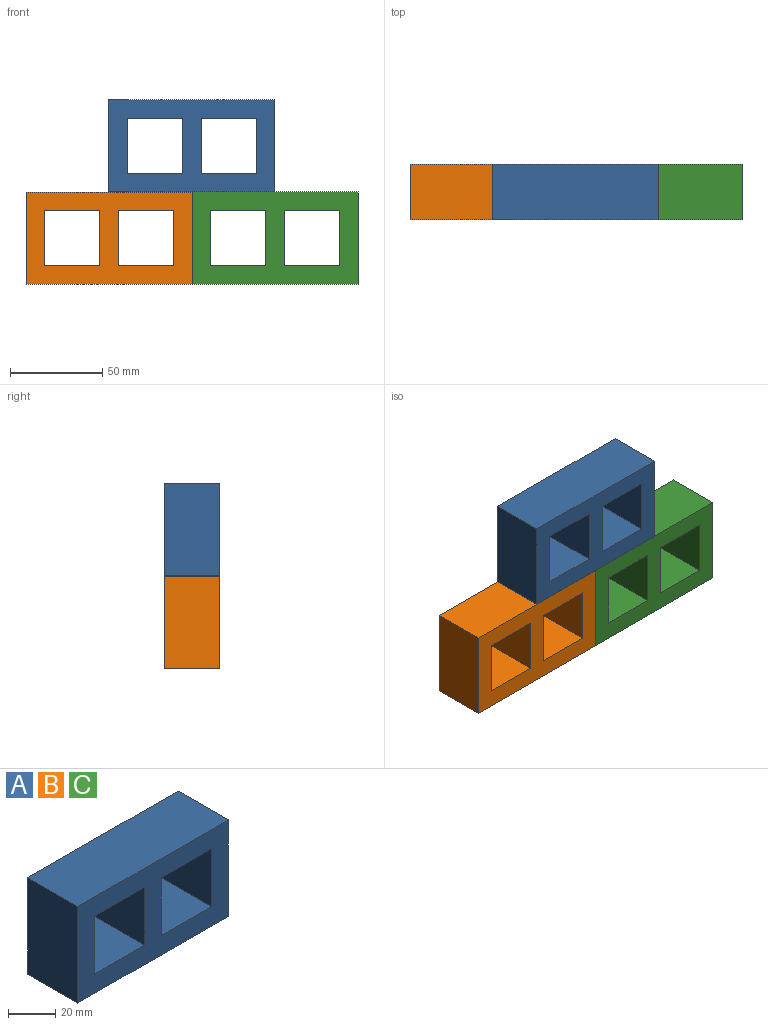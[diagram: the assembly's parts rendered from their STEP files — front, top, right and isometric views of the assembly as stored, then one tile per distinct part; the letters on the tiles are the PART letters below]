
ASSEMBLY  parts=3 mates=2
PART A: 14 faces, bbox 90x30x50 mm
  f0: plane 90x30mm, normal (0,0,1), area 2700mm2, adj f1,f11,f12,f13
  f1: plane 50x30mm, normal (-1,0,0), area 1500mm2, adj f0,f2,f12,f13
  f2: plane 90x30mm, normal (0,0,-1), area 2700mm2, adj f1,f11,f12,f13
  f3: plane 30x30mm, normal (1,0,0), area 900mm2, adj f4,f9,f12,f13
  f4: plane 30x30mm, normal (0,0,-1), area 900mm2, adj f3,f5,f12,f13
  f5: plane 30x30mm, normal (-1,0,0), area 900mm2, adj f4,f9,f12,f13
  f6: plane 30x30mm, normal (1,0,0), area 900mm2, adj f7,f10,f12,f13
  f7: plane 30x30mm, normal (0,0,-1), area 900mm2, adj f6,f8,f12,f13
  f8: plane 30x30mm, normal (-1,0,0), area 900mm2, adj f7,f10,f12,f13
  f9: plane 30x30mm, normal (0,0,1), area 900mm2, adj f3,f5,f12,f13
  f10: plane 30x30mm, normal (0,0,1), area 900mm2, adj f6,f8,f12,f13
  f11: plane 50x30mm, normal (1,0,0), area 1500mm2, adj f0,f2,f12,f13
  f12: plane 90x50mm, normal (0,-1,0), area 2700mm2, adj f0,f1,f2,f3,f4,f5,f6,f7
  f13: plane 90x50mm, normal (0,1,0), area 2700mm2, adj f0,f1,f2,f3,f4,f5,f6,f7
PART B: same geometry as A
PART C: same geometry as A
PLACE A t=(40.95,30.79,74.97)mm
PLACE B t=(-4.05,30.79,24.97)mm
PLACE C rot(axis=(0,1,0),180deg) t=(95.95,30.79,20.76)mm fixed
MATE fastened A.f2 <-> C.f2  axis (0,0,-1) through (45.95,15.79,47.86)mm
MATE fastened C.f11 <-> B.f11  axis (-1,0,0) through (45.95,15.79,22.86)mm
